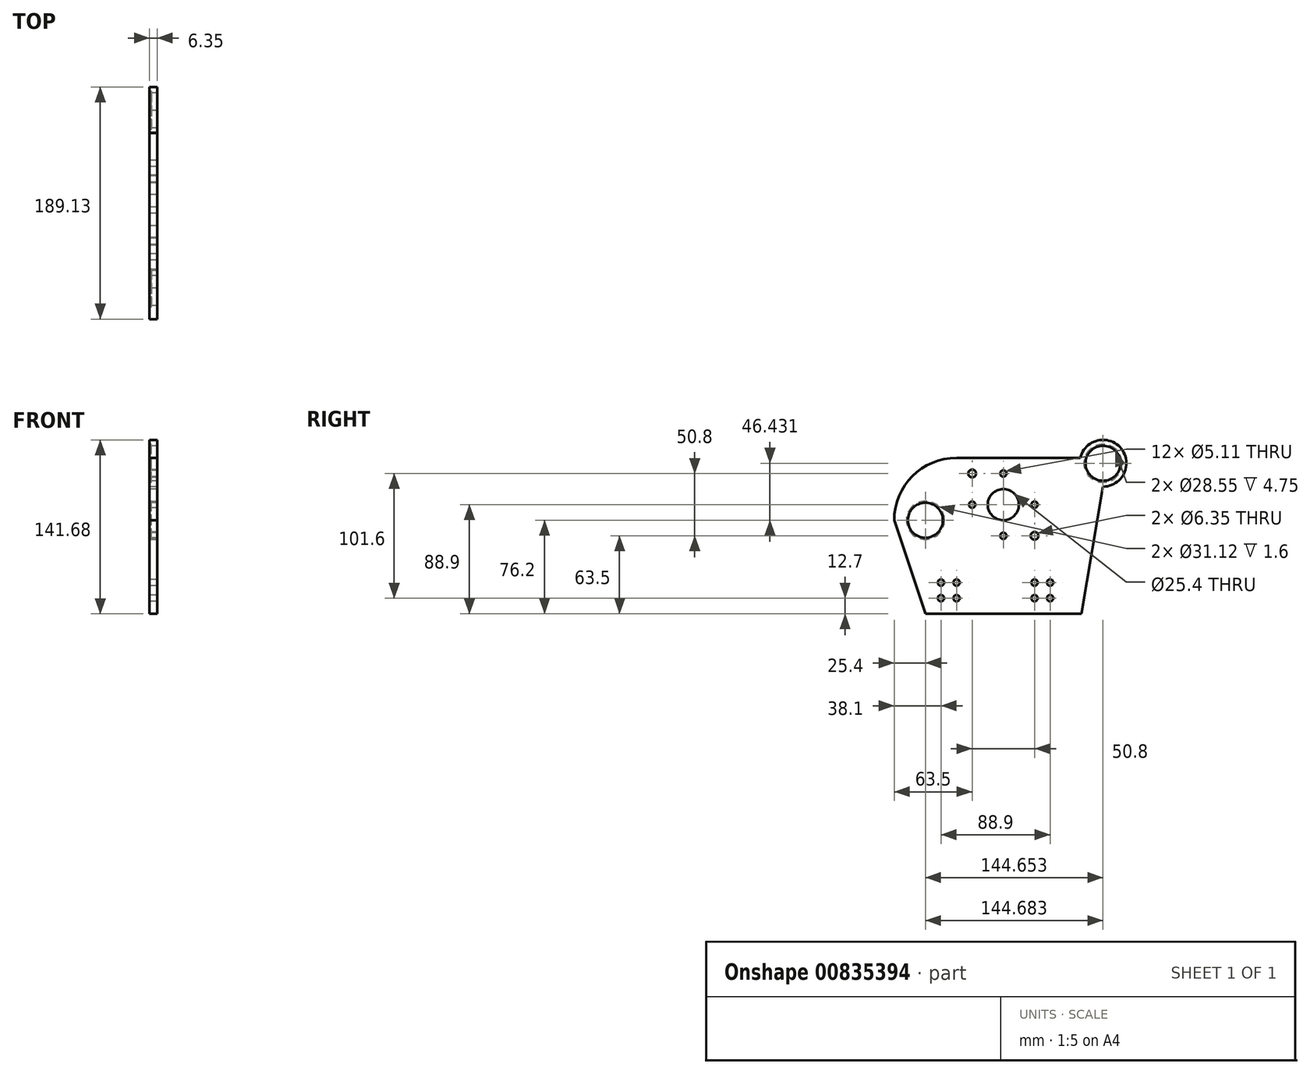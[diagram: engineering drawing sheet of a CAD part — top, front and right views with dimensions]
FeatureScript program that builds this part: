
annotation { "Feature Type Name" : "Feature", "Feature Type Description" : "" }
export const myFeature = defineFeature(function(context is Context, id is Id, definition is map)
    precondition{}
    {
        {
            var Q0;
            Q0=qCreatedBy(makeId("Right.planeOp"),FACE);
            var sketch = newSketch(context, id + "F0", { "sketchPlane" : qUnion([Q0])});
            skLineSegment(sketch, "E0.top", {"start": v(25.4, 127) * mm, "end": v(126.14, 127) * mm});
            skLineSegment(sketch, "E1", {"start": v(-25.4, 76.2) * mm, "end": v(0, 0) * mm});
            skArc(sketch, "E2", {"start": v(25.4, 127) * mm, "mid": v(-10.52, 112.12) * mm, "end": v(-25.4, 76.2) * mm});
            skPoint(sketch, "E3.end.orphan", {"position": v(144.68, 128.98) * mm});
            skPoint(sketch, "E4.end.orphan", {"position": v(141.66, 128.98) * mm});
            skPoint(sketch, "E5.end.orphan", {"position": v(136.5, 122.63) * mm});
            skPoint(sketch, "E6.start.orphan", {"position": v(147.67, 128.98) * mm});
            skPoint(sketch, "E7.start.orphan", {"position": v(152.9, 122.63) * mm});
            skPoint(sketch, "E8.orphan", {"position": v(147.67, 116.28) * mm});
            skLineSegment(sketch, "E9.2", {"start": v(148.32, 116.28) * mm, "end": v(147.67, 116.28) * mm});
            skPoint(sketch, "E9.0.midPoint", {"position": v(150.17, 125.8) * mm});
            skPoint(sketch, "E10.orphan", {"position": v(144.68, 122.63) * mm});
            skArc(sketch, "E11", {"start": v(144.68, 103.58) * mm, "mid": v(159.62, 134.46) * mm, "end": v(126.14, 127) * mm});
            skLineSegment(sketch, "E12", {"start": v(144.68, 103.58) * mm, "end": v(127, 0) * mm});
            skCircle(sketch, "E13", {"center": v(0, 76.2) * mm, "radius": 14.27 * mm});
            skCircle(sketch, "E14", {"center": v(38.1, 114.3) * mm, "radius": 3.18 * mm});
            skCircle(sketch, "E15", {"center": v(63.5, 88.9) * mm, "radius": 12.7 * mm});
            skCircle(sketch, "E16", {"center": v(63.5, 114.3) * mm, "radius": 2.55 * mm});
            skCircle(sketch, "E17", {"center": v(38.1, 88.9) * mm, "radius": 2.55 * mm});
            skCircle(sketch, "E18", {"center": v(88.9, 88.9) * mm, "radius": 2.55 * mm});
            skCircle(sketch, "E19", {"center": v(63.5, 63.5) * mm, "radius": 2.55 * mm});
            skCircle(sketch, "E20", {"center": v(88.9, 63.5) * mm, "radius": 3.18 * mm});
            skLineSegment(sketch, "E21.bottom", {"start": v(0, 0) * mm, "end": v(12.7, 0) * mm});
            skPoint(sketch, "E22.end.orphan", {"position": v(10.05, 0) * mm});
            skCircle(sketch, "E23", {"center": v(101.6, 25.4) * mm, "radius": 2.55 * mm});
            skCircle(sketch, "E24", {"center": v(101.6, 12.7) * mm, "radius": 2.55 * mm});
            skCircle(sketch, "E25", {"center": v(88.9, 25.4) * mm, "radius": 2.55 * mm});
            skCircle(sketch, "E26", {"center": v(88.9, 12.7) * mm, "radius": 2.55 * mm});
            skCircle(sketch, "E27", {"center": v(12.7, 25.4) * mm, "radius": 2.55 * mm});
            skCircle(sketch, "E28", {"center": v(12.7, 12.7) * mm, "radius": 2.55 * mm});
            skLineSegment(sketch, "E29.trimOffspring", {"start": v(12.7, 0) * mm, "end": v(25.4, 0) * mm});
            skCircle(sketch, "E30", {"center": v(25.4, 25.4) * mm, "radius": 2.55 * mm});
            skCircle(sketch, "E31", {"center": v(25.4, 12.7) * mm, "radius": 2.55 * mm});
            skPoint(sketch, "E32.orphan", {"position": v(25.4, 0) * mm});
            skLineSegment(sketch, "E33.trimOffspring", {"start": v(25.4, 0) * mm, "end": v(101.6, 0) * mm});
            skLineSegment(sketch, "E34.trimOffspring", {"start": v(101.6, 0) * mm, "end": v(127, 0) * mm});
            skPoint(sketch, "E35.orphan", {"position": v(148.35, 128.98) * mm});
            skPoint(sketch, "E9.1.start.orphan", {"position": v(151.99, 122.63) * mm});
            skCircle(sketch, "E36", {"center": v(144.68, 122.63) * mm, "radius": 14.27 * mm});
            skPoint(sketch, "E37.center.orphan", {"position": v(38.1, 63.5) * mm});
            skPoint(sketch, "E38.center.orphan", {"position": v(88.9, 114.3) * mm});
            skSolve(sketch);
        }
        {
            var Q0;
            Q0=qSketchRegion(id+"F0",true);
            extrude(context, id + "F1", {"entities" : qUnion([Q0]), "depth" : 6.35 * mm, "offsetDistance" : 25.4 * mm});
        }
        {
            var Q0;
            Q0=qCreatedBy(makeId("Right.planeOp"),FACE);
            var sketch = newSketch(context, id + "F2", { "sketchPlane" : qUnion([Q0])});
            skCircle(sketch, "E39", {"center": v(0, 76.2) * mm, "radius": 15.56 * mm});
            skCircle(sketch, "E40", {"center": v(144.65, 122.63) * mm, "radius": 15.56 * mm});
            skSolve(sketch);
        }
        {
            var Q0;
            Q0 = qSketchRegion(id + "F2", true);
            extrude(context, id + "F3", {"entities" : qUnion([Q0]), "operationType" : NewBodyOperationType.REMOVE, "depth" : 1.6 * mm, "offsetDistance" : 25.4 * mm});
        }
    });
